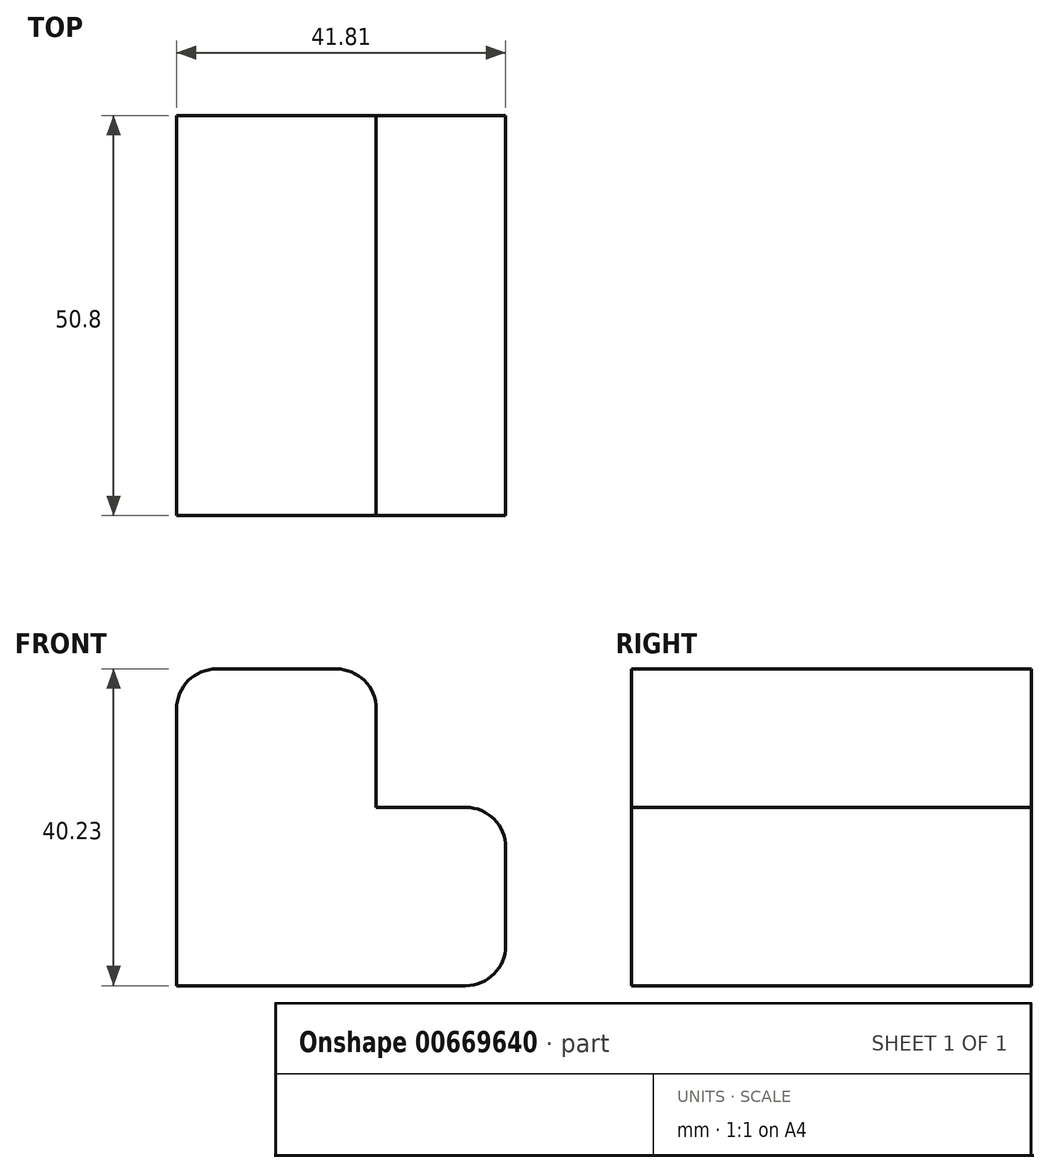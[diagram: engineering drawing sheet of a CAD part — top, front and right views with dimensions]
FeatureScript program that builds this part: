
annotation { "Feature Type Name" : "Feature", "Feature Type Description" : "" }
export const myFeature = defineFeature(function(context is Context, id is Id, definition is map)
    precondition{}
    {
        {
            var Q0;
            Q0=qCreatedBy(makeId("Front.planeOp"),FACE);
            var sketch = newSketch(context, id + "F0", { "sketchPlane" : qUnion([Q0])});
            skLineSegment(sketch, "E0", {"start": v(0, 0) * mm, "end": v(0, 40.23) * mm});
            skLineSegment(sketch, "E1", {"start": v(0, 40.23) * mm, "end": v(25.36, 40.23) * mm});
            skLineSegment(sketch, "E2", {"start": v(25.36, 40.23) * mm, "end": v(25.36, 22.65) * mm});
            skLineSegment(sketch, "E3", {"start": v(25.36, 22.65) * mm, "end": v(41.8, 22.65) * mm});
            skLineSegment(sketch, "E4", {"start": v(41.8, 22.65) * mm, "end": v(41.8, 0) * mm});
            skLineSegment(sketch, "E5", {"start": v(41.8, 0) * mm, "end": v(0, 0) * mm});
            skSolve(sketch);
        }
        {
            var Q0;
            Q0 = qSketchRegion(id + "F0", true);
            extrude(context, id + "F1", {"entities" : qUnion([Q0]), "depth" : 50.8 * mm, "offsetDistance" : 25.4 * mm});
        }
        {
            var Q0;
            Q0=makeQuery(id+"F1.opExtrude","SWEPT_EDGE",EDGE,{"disambiguationData":[OSD([sQuery(id+"F0.wireOp",EDGE,"E1"),sQuery(id+"F0.wireOp",EDGE,"E2")])]});
            var Q1;
            Q1=makeQuery(id+"F1.opExtrude","SWEPT_EDGE",EDGE,{"disambiguationData":[OSD([sQuery(id+"F0.wireOp",EDGE,"E3"),sQuery(id+"F0.wireOp",EDGE,"E4")])]});
            var Q2;
            Q2=makeQuery(id+"F1.opExtrude","SWEPT_EDGE",EDGE,{"disambiguationData":[OSD([sQuery(id+"F0.wireOp",EDGE,"E4"),sQuery(id+"F0.wireOp",EDGE,"E5")])]});
            var Q3;
            Q3=makeQuery(id+"F1.opExtrude","SWEPT_EDGE",EDGE,{"disambiguationData":[OSD([sQuery(id+"F0.wireOp",EDGE,"E0"),sQuery(id+"F0.wireOp",EDGE,"E1")])]});
            fillet(context, id + "F2", {"entities" : qUnion([Q0, Q1, Q2, Q3]), "radius" : 5.08 * mm, "tangentPropagation" : true, "allowEdgeOverflow" : false});
        }
    });
